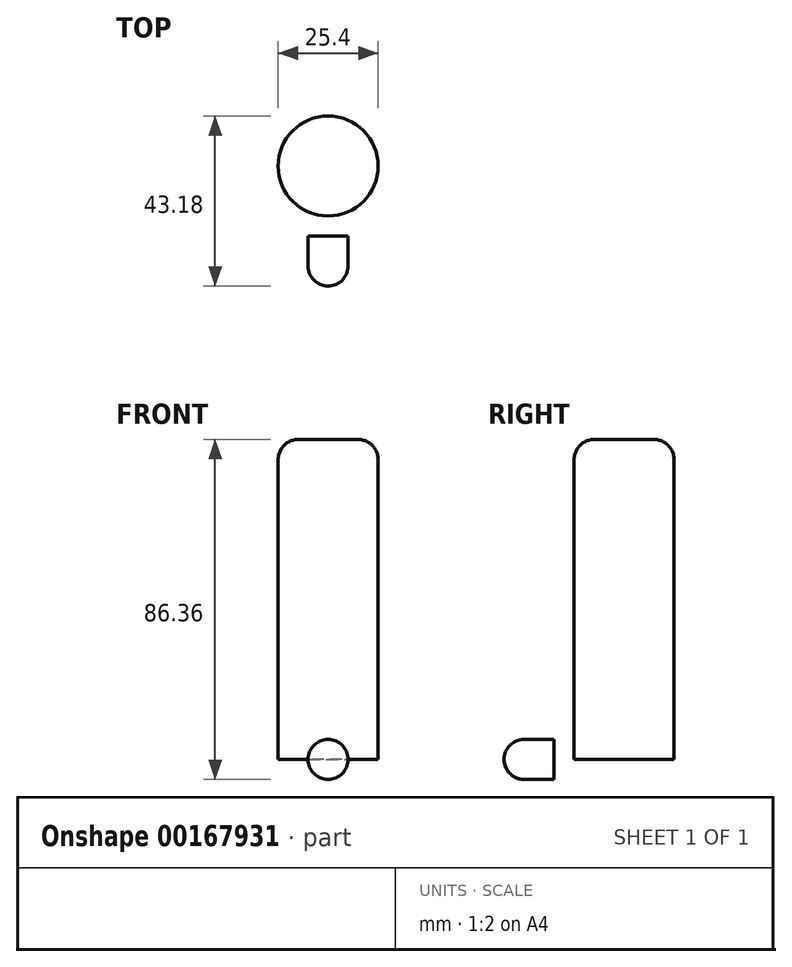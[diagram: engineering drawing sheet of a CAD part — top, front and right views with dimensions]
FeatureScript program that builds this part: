
annotation { "Feature Type Name" : "Feature", "Feature Type Description" : "" }
export const myFeature = defineFeature(function(context is Context, id is Id, definition is map)
    precondition{}
    {
        {
            var Q0;
            Q0=qCreatedBy(makeId("Top.planeOp"),FACE);
            var sketch = newSketch(context, id + "F0", { "sketchPlane" : qUnion([Q0])});
            skCircle(sketch, "E0", {"center": v(0, 0) * mm, "radius": 12.7 * mm});
            skLineSegment(sketch, "E1", {"start": v(12.7, 0) * mm, "end": v(31.75, 0) * mm});
            skSolve(sketch);
        }
        {
            var Q0;
            Q0=makeQuery(id+"F0.imprint","IMPRINT",FACE,{"disambiguationData":[TD([[makeQuery(id+"F0.imprint","IMPRINT",EDGE,{"derivedFrom":sQuery(id+"F0.wireOp",EDGE,"E0")}),1.0]])]});
            extrude(context, id + "F1", {"entities" : qUnion([Q0]), "depth" : 76.2 * mm});
        }
        {
            var Q0;
            Q0=makeQuery(id+"F1.opExtrude","CAP_FACE",FACE,{"disambiguationData":[OSD([sQuery(id+"F0.wireOp",EDGE,"E0")])],"isStart":false});
            extrude(context, id + "F2", {"entities" : qUnion([Q0]), "operationType" : NewBodyOperationType.ADD, "depth" : 5.08 * mm});
        }
        {
            var Q0;
            Q0=makeQuery(id+"F2.opExtrude","CAP_EDGE",EDGE,{"disambiguationData":[OSD([sQuery(id+"F0.wireOp",EDGE,"E0")])],"isStart":false});
            fillet(context, id + "F3", {"entities" : qUnion([Q0]), "radius" : 5.08 * mm, "tangentPropagation" : true, "allowEdgeOverflow" : false});
        }
        {
            var Q0;
            Q0=qCreatedBy(makeId("Front.planeOp"),FACE);
            cPlane(context, id + "F4", {"entities" : qUnion([Q0]), "cplaneType" : CPlaneType.OFFSET, "offset" : 12.7 * mm, "width" : 152.4 * mm, "height" : 152.4 * mm});
        }
        {
            var Q0;
            Q0=qCreatedBy(id+"F4.planeOp",FACE);
            var sketch = newSketch(context, id + "F5", { "sketchPlane" : qUnion([Q0])});
            skLineSegment(sketch, "E2", {"start": v(0, 1.58) * mm, "end": v(0, 65.53) * mm});
            skSolve(sketch);
        }
        {
            var Q0;
            Q0 = qSketchRegion(id + "F5", true);
            var Q1;
            Q1=sQuery(id+"F5.wireOp",EDGE,"E2");
            extrude(context, id + "F6", {"entities" : qUnion([Q0]), "bodyType" : ToolBodyType.SURFACE, "surfaceEntities" : qUnion([Q1]), "depth" : 5.08 * mm});
        }
        {
            var Q0;
            Q0=makeQuery(id+"F6.opExtrude","CAP_EDGE",EDGE,{"disambiguationData":[OSD([sQuery(id+"F5.wireOp",EDGE,"E2")])],"isStart":false});
            cPoint(context, id + "F7", {"entities" : qUnion([Q0]), "parameter" : 0.5});
        }
        {
            var Q0;
            Q0=qCreatedBy(makeId("Front.planeOp"),FACE);
            var Q1;
            Q1 = qCreatedBy(id + "F7" ,VERTEX);
            cPlane(context, id + "F8", {"entities" : qUnion([Q0, Q1]), "cplaneType" : CPlaneType.PLANE_POINT, "offset" : 25.4 * mm, "width" : 152.4 * mm, "height" : 152.4 * mm});
        }
        {
            var Q0;
            Q0=qCreatedBy(id+"F8.planeOp",FACE);
            var sketch = newSketch(context, id + "F9", { "sketchPlane" : qUnion([Q0])});
            skCircle(sketch, "E3", {"center": v(0, 0) * mm, "radius": 5.08 * mm});
            skSolve(sketch);
        }
        {
            var Q0;
            Q0=makeQuery(id+"F9.imprint","IMPRINT",FACE,{"disambiguationData":[TD([[makeQuery(id+"F9.imprint","IMPRINT",EDGE,{"derivedFrom":sQuery(id+"F9.wireOp",EDGE,"E3")}),1.0]])]});
            extrude(context, id + "F10", {"entities" : qUnion([Q0]), "depth" : 12.7 * mm});
        }
        {
            var Q0;
            Q0=makeQuery(id+"F10.opExtrude","CAP_EDGE",EDGE,{"disambiguationData":[OSD([sQuery(id+"F9.wireOp",EDGE,"E3")])],"isStart":false});
            fillet(context, id + "F11", {"entities" : qUnion([Q0]), "radius" : 5.08 * mm, "tangentPropagation" : true, "allowEdgeOverflow" : false});
        }
    });
